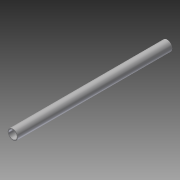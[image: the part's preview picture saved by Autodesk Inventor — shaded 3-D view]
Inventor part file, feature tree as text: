
AUTODESK INVENTOR PART (.ipt)
format: ipt  version: 2015 (Build 190159000, 159)  size: 73,216 bytes
history: native  units: in
note: dims shown in document units (in); Inventor stores cm internally (conversion verified against a paired STEP export)
features: extrude x1, sketch x1
ambient origin geometry x8: Origin, YZ Plane, XZ Plane, XY Plane, X Axis, Y Axis, Z Axis, Center Point
bodies: Solid1 (feature_tree)
feature tree (2):
  extrude  "Extrusion1"  Depth=19.0in
  sketch  "Sketch1"  dims[d0=1.25in d1=0.12in d2=19.0in d3=0.0in]
